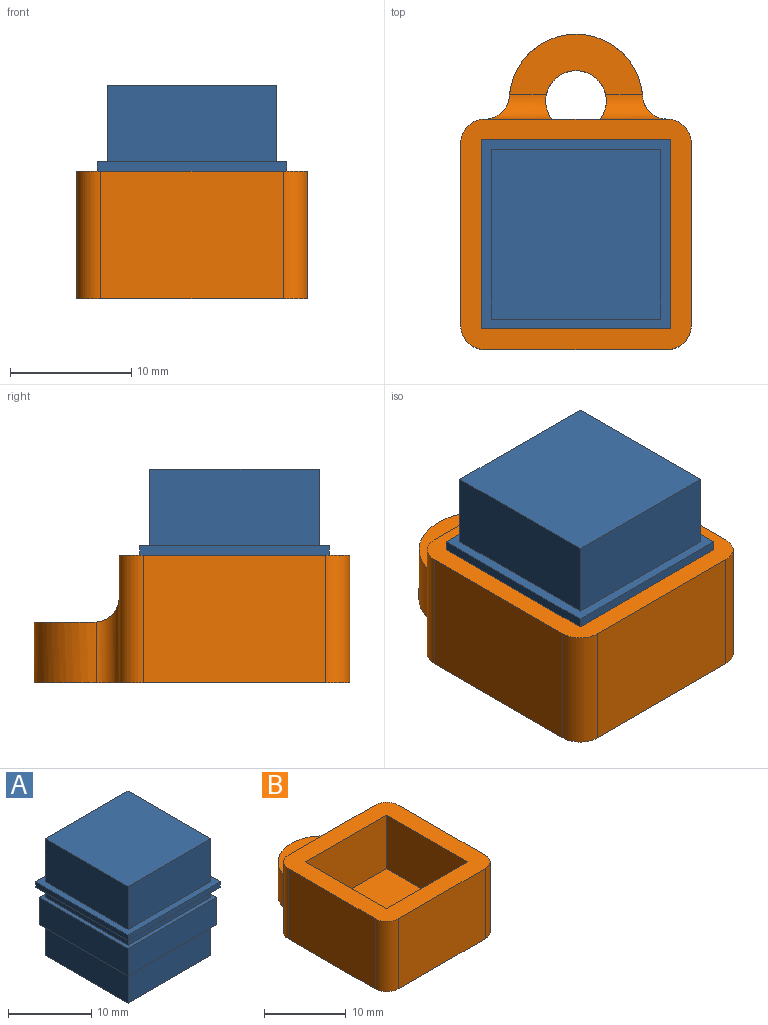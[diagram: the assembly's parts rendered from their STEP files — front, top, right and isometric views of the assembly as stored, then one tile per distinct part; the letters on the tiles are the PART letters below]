
ASSEMBLY  parts=2 mates=1
PART A: 26 faces, bbox 15.6x15.6x17.1 mm
  f0: plane 15.6x15.6mm, normal (0,0,1), area 47.4mm2, adj f5,f6,f7,f8,f10,f11,f12,f13
  f1: plane 14x1.5mm, normal (-1,0,0), area 21mm2, adj f2,f4,f9,f16
  f2: plane 14x1.5mm, normal (0,-1,0), area 21mm2, adj f1,f3,f9,f16
  f3: plane 14x1.5mm, normal (1,0,0), area 21mm2, adj f2,f4,f9,f16
  f4: plane 14x1.5mm, normal (0,1,0), area 21mm2, adj f1,f3,f9,f16
  f5: plane 15.6x0.8mm, normal (0,1,0), area 12.5mm2, adj f0,f6,f8,f9
  f6: plane 15.6x0.8mm, normal (-1,0,0), area 12.5mm2, adj f0,f5,f7,f9
  f7: plane 15.6x0.8mm, normal (0,-1,0), area 12.5mm2, adj f0,f6,f8,f9
  f8: plane 15.6x0.8mm, normal (1,0,0), area 12.5mm2, adj f0,f5,f7,f9
  f9: plane 15.6x15.6mm, normal (0,0,-1), area 47.4mm2, adj f1,f2,f3,f4,f5,f6,f7,f8
  f10: plane 14x6.3mm, normal (-1,0,0), area 88.2mm2, adj f0,f11,f13,f14
  f11: plane 14x6.3mm, normal (0,-1,0), area 88.2mm2, adj f0,f10,f12,f14
  f12: plane 14x6.3mm, normal (1,0,0), area 88.2mm2, adj f0,f11,f13,f14
  f13: plane 14x6.3mm, normal (0,1,0), area 88.2mm2, adj f0,f10,f12,f14
  f14: plane 14x14mm, normal (0,0,1), area 196mm2, adj f10,f11,f12,f13
  f15: plane 15x15mm, normal (0,0,-1), area 29mm2, adj f17,f18,f19,f20,f22,f23,f24,f25
  f16: plane 15x15mm, normal (0,0,1), area 29mm2, adj f1,f2,f3,f4,f17,f18,f19,f20
  f17: plane 15x4mm, normal (0,-1,0), area 60mm2, adj f15,f16,f18,f20
  f18: plane 15x4mm, normal (1,0,0), area 60mm2, adj f15,f16,f17,f19
  f19: plane 15x4mm, normal (0,1,0), area 60mm2, adj f15,f16,f18,f20
  f20: plane 15x4mm, normal (-1,0,0), area 60mm2, adj f15,f16,f17,f19
  f21: plane 14x14mm, normal (0,0,-1), area 196mm2, adj f22,f23,f24,f25
  f22: plane 14x4.5mm, normal (0,1,0), area 63mm2, adj f15,f21,f23,f25
  f23: plane 14x4.5mm, normal (1,0,0), area 63mm2, adj f15,f21,f22,f24
  f24: plane 14x4.5mm, normal (0,-1,0), area 63mm2, adj f15,f21,f23,f25
  f25: plane 14x4.5mm, normal (-1,0,0), area 63mm2, adj f15,f21,f22,f24
PART B: 22 faces, bbox 19x26x10.5 mm
  f0: plane 15x10.5mm, normal (0,1,0), area 80.7mm2, adj f1,f3,f11,f14,f15,f16,f17,f18
  f1: plane 19x19mm, normal (0,0,1), area 161.6mm2, adj f0,f2,f4,f5,f6,f7,f9,f10
  f2: plane 15x10.5mm, normal (-1,0,0), area 157.5mm2, adj f1,f3,f18,f20
  f3: plane 26x19mm, normal (0,0,-1), area 406.4mm2, adj f0,f2,f4,f5,f11,f12,f14,f16
  f4: plane 15x10.5mm, normal (1,0,0), area 157.5mm2, adj f1,f3,f19,f21
  f5: plane 15x10.5mm, normal (0,-1,0), area 157.5mm2, adj f1,f3,f20,f21
  f6: plane 14x8mm, normal (1,0,0), area 112mm2, adj f1,f7,f8,f10
  f7: plane 14x8mm, normal (0,-1,0), area 112mm2, adj f1,f6,f8,f9
  f8: plane 14x14mm, normal (0,0,1), area 196mm2, adj f6,f7,f9,f10
  f9: plane 14x8mm, normal (-1,0,0), area 112mm2, adj f1,f7,f8,f10
  f10: plane 14x8mm, normal (0,1,0), area 112mm2, adj f1,f6,f8,f9
  f11: cylinder r=2.5mm len=7mm, axis (0,0,-1), area 57.3mm2, adj f0,f3,f13,f15,f17
  f12: cylinder r=5.5mm len=10.98mm, axis (0,0,-1), area 82.7mm2, adj f3,f13,f14,f15,f16,f17
  f13: plane 10.95x5mm, normal (0,0,1), area 34.7mm2, adj f11,f12,f15,f17
  f14: cylinder r=2mm len=7mm, axis (0,0,-1), area 17.3mm2, adj f0,f3,f12,f15
  f15: cylinder r=2mm len=5.48mm, axis (-1,0,0), area 12.3mm2, adj f0,f11,f12,f13,f14
  f16: cylinder r=2mm len=7mm, axis (0,0,-1), area 17.3mm2, adj f0,f3,f12,f17
  f17: cylinder r=2mm len=5.48mm, axis (-1,0,0), area 12.3mm2, adj f0,f11,f12,f13,f16
  f18: cylinder r=2mm len=10.5mm, axis (0,0,-1), area 33mm2, adj f0,f1,f2,f3
  f19: cylinder r=2mm len=10.5mm, axis (0,0,1), area 33mm2, adj f0,f1,f3,f4
  f20: cylinder r=2mm len=10.5mm, axis (0,0,1), area 33mm2, adj f1,f2,f3,f5
  f21: cylinder r=2mm len=10.5mm, axis (0,0,-1), area 33mm2, adj f1,f3,f4,f5
PLACE A t=(-8.42,-9.06,12.03)mm
PLACE B t=(-1.42,-2.06,4.03)mm
MATE fastened A.f9 <-> B.f1  axis (0,0,-1) through (-1.42,-2.06,12.03)mm
